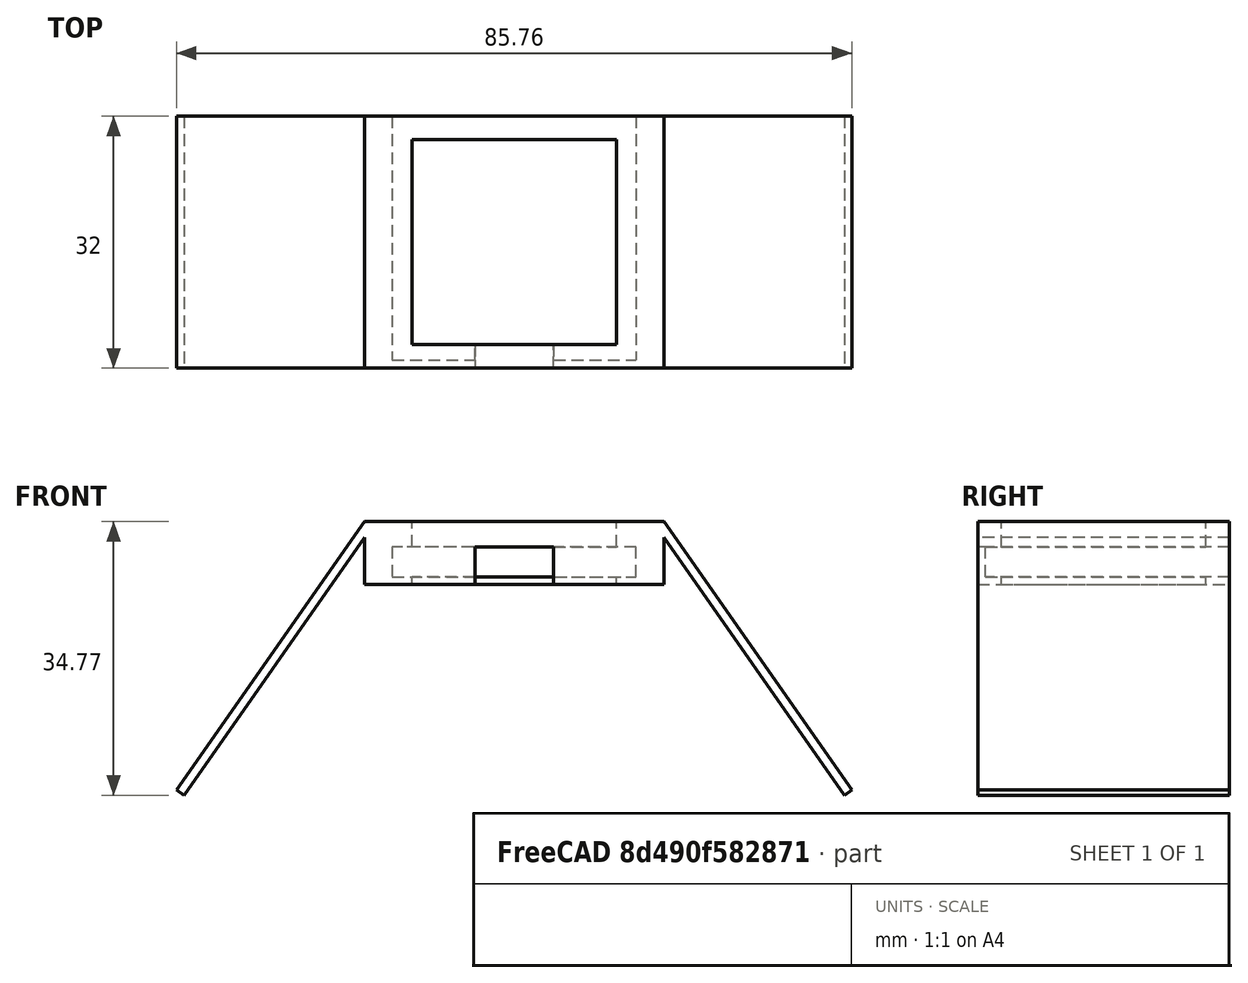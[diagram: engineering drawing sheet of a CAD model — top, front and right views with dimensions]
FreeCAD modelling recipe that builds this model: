
FCSTD DOCUMENT  (FreeCAD 0.17R13541 (Git))
Label: TubeSlitHolder_Plus_MirrorHolders
License: All rights reserved
LicenseURL: http://en.wikipedia.org/wiki/All_rights_reserved
objects: Sketcher::SketchObject×6, PartDesign::Pad×3, PartDesign::Pocket×3, PartDesign::Body×1, Mesh::Feature×1
note: 19 computed .brp shape members not serialized (recipe doc carries the construction recipe); baked Part::Feature solids carry a one-line shape summary decoded from their .brp

FEATURE [Sketcher::SketchObject] Sketch
  MapMode = 5
  Support = -> [XY_Plane]
  sketch-geometry (4):
    g0: LineSegment StartX=-38 StartY=0 StartZ=0 EndX=0 EndY=0 EndZ=0
    g1: LineSegment StartX=0 StartY=0 StartZ=0 EndX=0 EndY=-32 EndZ=0
    g2: LineSegment StartX=0 StartY=-32 StartZ=0 EndX=-38 EndY=-32 EndZ=0
    g3: LineSegment StartX=-38 StartY=-32 StartZ=0 EndX=-38 EndY=0 EndZ=0
  constraints (11):
    c: Coincident(g0,g1)
    c: Coincident(g1,g2)
    c: Coincident(g2,g3)
    c: Coincident(g3,g0)
    c: Horizontal(g0)
    c: Horizontal(g2)
    c: Vertical(g1)
    c: Vertical(g3)
    c: Distance(g0) = 38
    c: Distance(g3) = 32
    c: Coincident(g0,g-1)
FEATURE [PartDesign::Pad] Pad
  Length = 8
  Length2 = 100
  Profile = -> Sketch
  Type = 0
FEATURE [Sketcher::SketchObject] Sketch001
  MapMode = 5
  Placement = pos=(0,0,0) rot=(0,0.707107,0.707107;3.14159rad)
  Support = -> [Pad]
  sketch-geometry (4):
    g0: LineSegment StartX=3.5 StartY=4.8 StartZ=0 EndX=34.5 EndY=4.8 EndZ=0
    g1: LineSegment StartX=34.5 StartY=4.8 StartZ=0 EndX=34.5 EndY=1 EndZ=0
    g2: LineSegment StartX=34.5 StartY=1 StartZ=0 EndX=3.5 EndY=1 EndZ=0
    g3: LineSegment StartX=3.5 StartY=1 StartZ=0 EndX=3.5 EndY=4.8 EndZ=0
  constraints (12):
    c: Coincident(g0,g1)
    c: Coincident(g1,g2)
    c: Coincident(g2,g3)
    c: Coincident(g3,g0)
    c: Horizontal(g0)
    c: Horizontal(g2)
    c: Vertical(g1)
    c: Vertical(g3)
    c: Distance(g0) = 31
    c: Distance(g3) = 3.8
    c: DistanceY(g-1,g2) = 1
    c: DistanceX(g-1,g2) = 3.5
FEATURE [PartDesign::Pocket] Pocket
  BaseFeature = -> Pad
  Length = 31
  Length2 = 100
  Profile = -> Sketch001
  Type = 0
FEATURE [Sketcher::SketchObject] Sketch002
  MapMode = 5
  Placement = pos=(0,0,0) rot=(1,0,0;3.14159rad)
  Support = -> [Pocket]
  sketch-geometry (4):
    g0: LineSegment StartX=-6 StartY=3 StartZ=0 EndX=-32 EndY=3 EndZ=0
    g1: LineSegment StartX=-32 StartY=3 StartZ=0 EndX=-32 EndY=29 EndZ=0
    g2: LineSegment StartX=-32 StartY=29 StartZ=0 EndX=-6 EndY=29 EndZ=0
    g3: LineSegment StartX=-6 StartY=29 StartZ=0 EndX=-6 EndY=3 EndZ=0
  constraints (12):
    c: Coincident(g0,g1)
    c: Coincident(g1,g2)
    c: Coincident(g2,g3)
    c: Coincident(g3,g0)
    c: Horizontal(g0)
    c: Horizontal(g2)
    c: Vertical(g1)
    c: Vertical(g3)
    c: Distance(g0) = 26
    c: Distance(g3) = 26
    c: DistanceX(g0,g-1) = 6
    c: DistanceY(g-1,g0) = 3
FEATURE [PartDesign::Pocket] Pocket001
  BaseFeature = -> Pocket
  Length = 20
  Length2 = 100
  Profile = -> Sketch002
  Type = 0
FEATURE [Sketcher::SketchObject] Sketch003
  MapMode = 5
  Placement = pos=(0,0,0) rot=(1,0,0;3.14159rad)
  Support = -> [Pocket001]
  sketch-geometry (4):
    g0: LineSegment StartX=-14 StartY=29 StartZ=0 EndX=-24 EndY=29 EndZ=0
    g1: LineSegment StartX=-24 StartY=29 StartZ=0 EndX=-24 EndY=32 EndZ=0
    g2: LineSegment StartX=-24 StartY=32 StartZ=0 EndX=-14 EndY=32 EndZ=0
    g3: LineSegment StartX=-14 StartY=32 StartZ=0 EndX=-14 EndY=29 EndZ=0
  constraints (12):
    c: Coincident(g0,g1)
    c: Coincident(g1,g2)
    c: Coincident(g2,g3)
    c: Coincident(g3,g0)
    c: Horizontal(g0)
    c: Horizontal(g2)
    c: Vertical(g1)
    c: Vertical(g3)
    c: Distance(g3) = 3
    c: Distance(g0) = 10
    c: DistanceY(g-1,g2) = 32
    c: DistanceX(g2,g-1) = 14
FEATURE [PartDesign::Pocket] Pocket002
  BaseFeature = -> Pocket001
  Length = 4.8
  Length2 = 100
  Profile = -> Sketch003
  Type = 0
FEATURE [Sketcher::SketchObject] Sketch004
  MapMode = 5
  Placement = pos=(0,0,0) rot=(0,0.707107,0.707107;3.14159rad)
  Support = -> [Pocket002]
  sketch-geometry (4):
    g0: LineSegment StartX=0 StartY=6 StartZ=0 EndX=-22.9431 EndY=-26.7661 EndZ=0
    g1: LineSegment StartX=-23.8828 StartY=-26.1081 StartZ=0 EndX=0 EndY=8 EndZ=0
    g2: LineSegment StartX=-23.8828 StartY=-26.1081 StartZ=0 EndX=-22.9431 EndY=-26.7661 EndZ=0
    g3: LineSegment StartX=0 StartY=8 StartZ=0 EndX=0 EndY=6 EndZ=0
  constraints (12):
    c: Angle(g0,g-2) = 0.610865
    c: DistanceY(g-1,g0) = 6
    c: DistanceX(g-1,g0) = 0
    c: Parallel(g1,g0)
    c: DistanceY(g-1,g1) = 8
    c: DistanceX(g-1,g1) = 0
    c: Coincident(g2,g1)
    c: Coincident(g2,g0)
    c: Perpendicular(g1,g2)
    c: Distance(g0) = 40
    c: Coincident(g3,g1)
    c: Coincident(g3,g0)
FEATURE [PartDesign::Pad] Pad001
  BaseFeature = -> Pocket002
  Length = 32
  Length2 = 100
  Profile = -> Sketch004
  Reversed = true
  Type = 0
FEATURE [Sketcher::SketchObject] Sketch005
  MapMode = 5
  Placement = pos=(0,0,0) rot=(0,0.707107,0.707107;3.14159rad)
  Support = -> [Pad001]
  sketch-geometry (4):
    g0: LineSegment StartX=60.9431 StartY=-26.7661 StartZ=0 EndX=38 EndY=6 EndZ=0
    g1: LineSegment StartX=38 StartY=8 StartZ=0 EndX=61.8828 EndY=-26.1081 EndZ=0
    g2: LineSegment StartX=60.9431 StartY=-26.7661 StartZ=0 EndX=61.8828 EndY=-26.1081 EndZ=0
    g3: LineSegment StartX=38 StartY=8 StartZ=0 EndX=38 EndY=6 EndZ=0
  constraints (12):
    c: Angle(g-1,g0) = 2.18166
    c: Distance(g0) = 40
    c: DistanceY(g-1,g0) = 6
    c: DistanceX(g-1,g0) = 38
    c: Parallel(g1,g0)
    c: DistanceX(g-1,g1) = 38
    c: DistanceY(g-1,g1) = 8
    c: Coincident(g2,g0)
    c: Coincident(g2,g1)
    c: Perpendicular(g1,g2)
    c: Coincident(g3,g1)
    c: Coincident(g3,g0)
FEATURE [PartDesign::Pad] Pad002
  BaseFeature = -> Pad001
  Length = 32
  Length2 = 100
  Profile = -> Sketch005
  Reversed = true
  Type = 0
FEATURE [PartDesign::Body] Body
  Group = -> [Sketch,Pad,Sketch001,Pocket,Sketch002,Pocket001,Sketch003,Pocket002,Sketch004,Pad001,Sketch005,Pad002]
  Origin = -> Origin
  Tip = -> Pad002
FEATURE [Mesh::Feature] Mesh  label="Pad002 (Meshed)"
